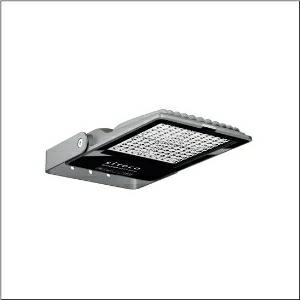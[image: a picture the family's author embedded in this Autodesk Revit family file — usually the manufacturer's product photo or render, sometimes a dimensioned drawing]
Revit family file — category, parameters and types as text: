
# Revit family: sicompact_31_mini___pl32_5xa7571b1k23_1e51
name_source: partatom
category: Lighting Fixtures
units: mm (PartAtom-declared; Revit-internal decimal feet)

## family parameters
Cut with Voids When Loaded = No
Host = Face
Light Source = No
Part Type = Normal
Room Calculation Point = No
Round Connector Dimension = Use Diameter
Shared = No

## types (1)
- SiCompact 31 mini  PL32 (1 x LED, 8000 lm, 48 W, 3000K)
    Apparent Load = 48 VA
    CIE Flux Codes = 32 69 98 100 100
    Color Rendering = 70
    Color Temperature = 3000K
    Default Elevation = 1800 mm
    Description = SiCompact 31 mini, floodlight, primary light control with lens, of plastic, of toughened safety glass, transparent, light distribution: PL32, light emission: direct distribution, primary light characteristic: asymmetric, installation type: surface-mounted, LED, High Power LED, rated luminous flux: 8.000lm, luminous efficacy: 167lm/W, light colour: 730, colour temperature: 3000K, control gear: ON/OFF, with cable, 3x 1.5mm², mains connection: 220..240V, AC, 50/60Hz, connection cable pre-assembled, cable length: 2m, rated input power: 48W, of diecast aluminium, specular, metallic grey (RAL 9006), length: 461mm, width: 261mm, height: 62mm, bracket, of sheet steel, coated, metallic grey (RAL 9006), ON/OFF, protection rating (complete): IP66, insulation class (complete): insulation class I (protective earthing), certification: CE, ENEC, impact resistance: IK08, permissible operating ambient temperature: -40..+45°C, packaging unit: 1 piece

Light Distribution: PL32
    Height = 62 mm  [stored 0.203412 ft]
    Lamp = 1 x LED
    Lamp Light Flux = 8000 lm
    Lamp Power = 48 W
    Lamp count = 1
    Length = 460 mm
    Luminous efficacy = 167 lm/W
    Manufacturer = Siteco
    ModVariant = No
    Model = 5XA7571B1K23
    Mounting Place = Wall
    Mounting Type = Surface mounted
    Number of Poles = 1
    OnlyDefault = Yes
    Power Factor = 1
    Product Name = SiCompact 31 mini | PL32
    Product group = floodlight | wall mounted
    ProductGroupID = 2002
    Protection Class = Protection class I
    Protection Degree = IP 66
    RLX_Detail_Level = 1
    RLX_Emergency_Light_Flux = 0 lm
    RLX_Emergency_Type = 0
    RLX_Emergency_Type_DB = No
    RlxData = <blob elided: 126553 chars, md5=f5447d9a>
    Socket = socket
    Standby Power = 0 W
    System Light Flux = 8000 lm
    System Power = 48 W
    Type Comments = Product without accessories
    Type Image = l_1006951.jpg
    URL = http://relux.com
    VarID = ---
    Voltage = 0 V
    Weight = 0.00 kg
    Width = 260 mm

note: [stored X ft] marks values corroborated as IEEE doubles in the binary element streams (Revit-internal decimal feet)

## geometry (parser evidence)
native form markers: Blend x4, Sweep x16
no freeform markers — native parametric forms only
